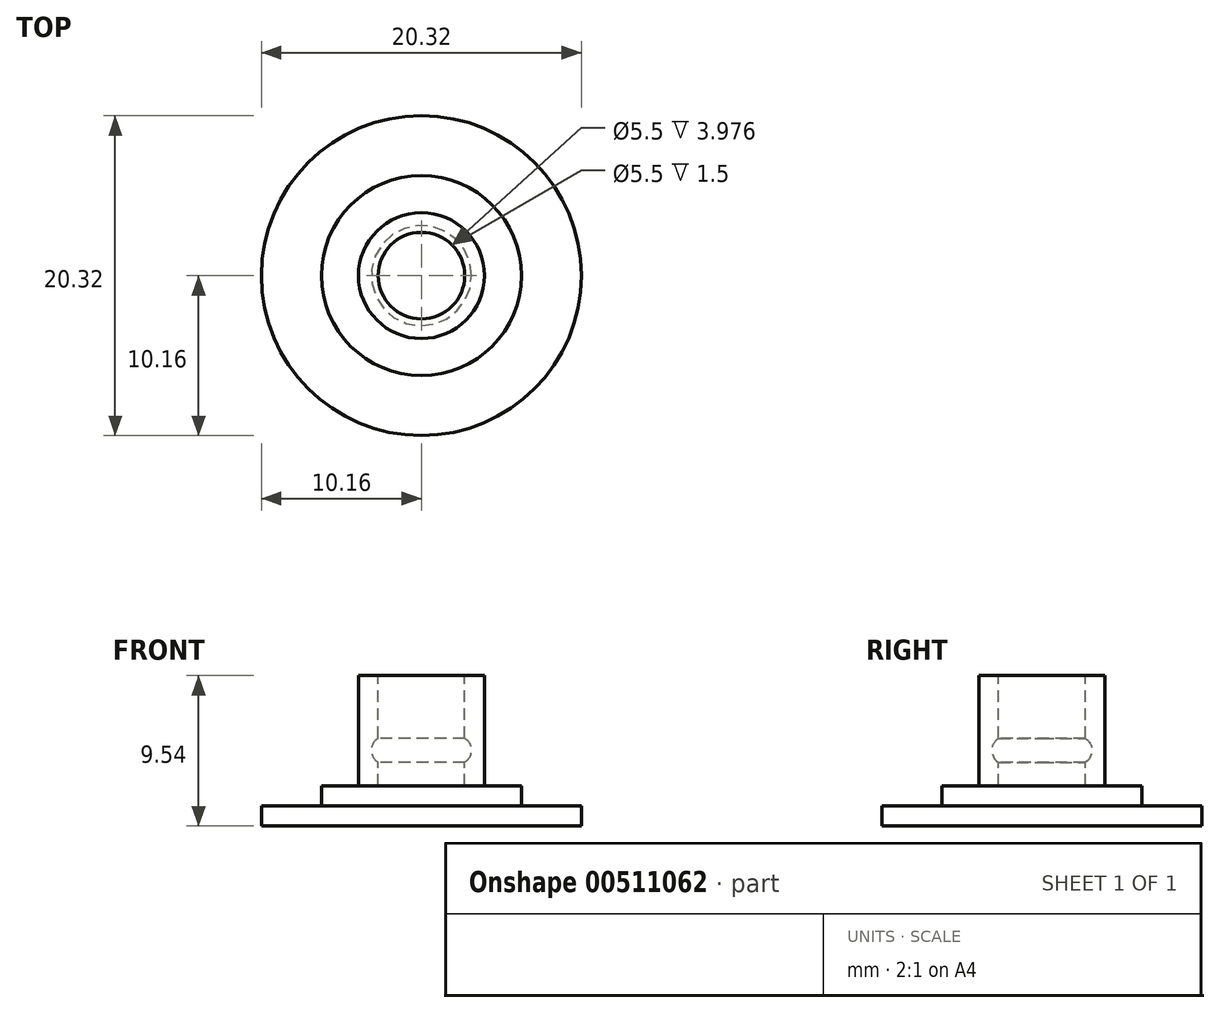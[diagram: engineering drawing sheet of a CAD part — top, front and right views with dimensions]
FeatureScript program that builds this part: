
annotation { "Feature Type Name" : "Feature", "Feature Type Description" : "" }
export const myFeature = defineFeature(function(context is Context, id is Id, definition is map)
    precondition{}
    {
        {
            var Q0;
            Q0=qCreatedBy(makeId("Front.planeOp"),FACE);
            var sketch = newSketch(context, id + "F0", { "sketchPlane" : qUnion([Q0])});
            skLineSegment(sketch, "E0", {"start": v(0, 0) * mm, "end": v(10.16, 0) * mm});
            skLineSegment(sketch, "E1", {"start": v(10.16, 0) * mm, "end": v(10.16, 2.54) * mm});
            skLineSegment(sketch, "E2", {"start": v(10.16, 2.54) * mm, "end": v(4, 2.54) * mm});
            skLineSegment(sketch, "E3", {"start": v(4, 2.54) * mm, "end": v(4, 9.54) * mm});
            skLineSegment(sketch, "E4", {"start": v(4, 9.54) * mm, "end": v(2.75, 9.54) * mm});
            skLineSegment(sketch, "E5", {"start": v(2.75, 9.54) * mm, "end": v(2.75, 5.56) * mm});
            skArc(sketch, "E6", {"start": v(2.75, 4.04) * mm, "mid": v(3.18, 4.8) * mm, "end": v(2.75, 5.56) * mm});
            skLineSegment(sketch, "E7", {"start": v(2.75, 4.04) * mm, "end": v(2.75, 2.54) * mm});
            skLineSegment(sketch, "E8", {"start": v(2.75, 2.54) * mm, "end": v(0, 2.54) * mm});
            skLineSegment(sketch, "E9", {"start": v(0, 2.54) * mm, "end": v(0, 0) * mm});
            skSolve(sketch);
        }
        {
            var Q0;
            Q0=makeQuery(id+"F0.imprint","IMPRINT",FACE,{"disambiguationData":[TD([[makeQuery(id+"F0.imprint","IMPRINT",EDGE,{"derivedFrom":sQuery(id+"F0.wireOp",EDGE,"E0")}),1.0]])]});
            var Q1;
            Q1=sQuery(id+"F0.wireOp",EDGE,"E9");
            revolve(context, id + "F1", {"entities" : qUnion([Q0]), "axis" : qUnion([Q1]), "revolveType" : RevolveType.FULL});
        }
        {
            var Q0;
            Q0=makeQuery(id+"F1.opRevolve","SWEPT_FACE",FACE,{"disambiguationData":[OSD([sQuery(id+"F0.wireOp",EDGE,"E2")])]});
            var sketch = newSketch(context, id + "F2", { "sketchPlane" : qUnion([Q0])});
            skCircle(sketch, "E10", {"center": v(0, 0) * mm, "radius": 6.35 * mm});
            skSolve(sketch);
        }
        {
            var Q0;
            Q0=makeQuery(id+"F2.imprint","IMPRINT",FACE,{"disambiguationData":[TD([[makeQuery(id+"F2.imprint","IMPRINT",EDGE,{"derivedFrom":sQuery(id+"F2.wireOp",EDGE,"E10")}),-1.0]])]});
            extrude(context, id + "F3", {"entities" : qUnion([Q0]), "operationType" : NewBodyOperationType.REMOVE, "oppositeDirection" : true, "depth" : 1.27 * mm, "offsetDistance" : 25.4 * mm});
        }
    });
